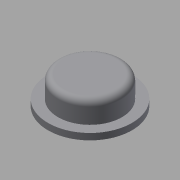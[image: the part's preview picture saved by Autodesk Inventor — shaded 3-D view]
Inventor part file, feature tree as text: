
AUTODESK INVENTOR PART (.ipt)
format: ipt  version: 2019 (Build 230136000, 136)  size: 140,288 bytes
history: native  units: mm
features: extrude x3, sketch x2, fillet x1
ambient origin geometry x8: Origin, YZ Plane, XZ Plane, XY Plane, X Axis, Y Axis, Z Axis, Center Point
bodies: Solid1 (feature_tree)
feature tree (6):
  sketch  "Sketch1"  dims[d0=10.5mm d1=8.0mm]
  extrude  "Extrusion1"  Depth=8.0mm
  extrude  "Extrusion2"  Depth=2.7mm TaperAngle=0.0deg
  fillet  "Fillet3"  Radius=0.75mm
  extrude  "Extrusion3"  Depth=2.0mm TaperAngle=0.0deg
  sketch  "Sketch2"  dims[d2=0.8mm d3=0.0mm d4=2.7mm d5=0.0mm d11=0.75mm d20=2.0mm d21=0.0mm]
